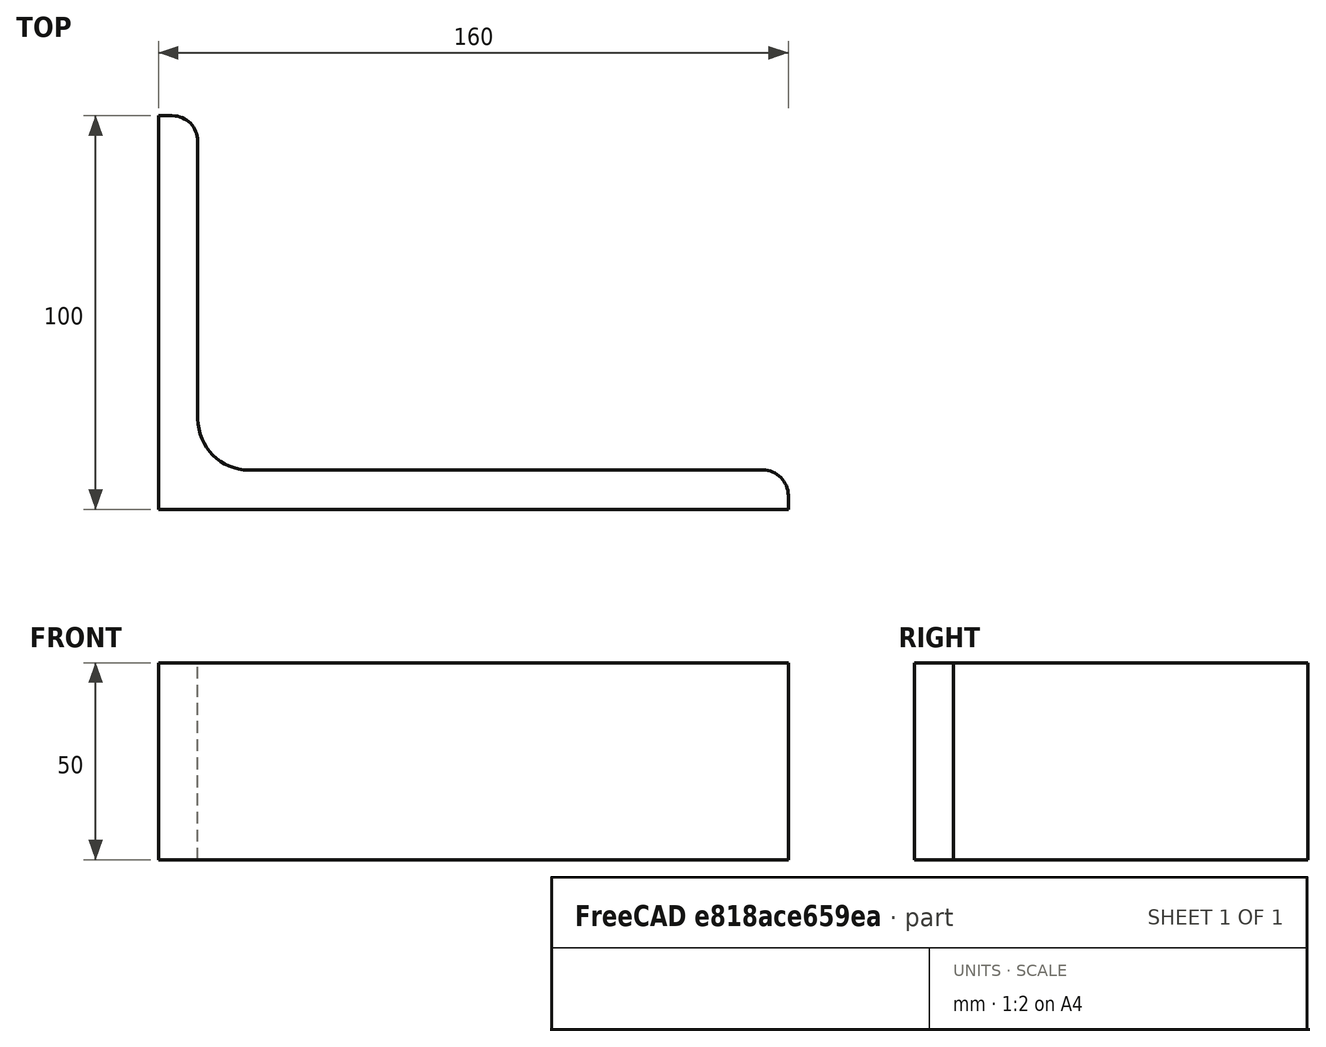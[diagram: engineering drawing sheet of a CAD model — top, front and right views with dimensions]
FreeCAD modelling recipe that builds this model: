
FCSTD DOCUMENT  (FreeCAD 0.15R4671 (Git))
Label: Angle Bar 160x100x10 EN10056 S235JR
License: All rights reserved
LicenseURL: http://en.wikipedia.org/wiki/All_rights_reserved
objects: Sketcher::SketchObject×1, Part::Extrusion×1
note: 2 computed .brp shape members not serialized (recipe doc carries the construction recipe); baked Part::Feature solids carry a one-line shape summary decoded from their .brp

FEATURE [Sketcher::SketchObject] Sketch
  sketch-geometry (9):
    g0: LineSegment StartX=0 StartY=0 StartZ=0 EndX=160 EndY=0 EndZ=0
    g1: LineSegment StartX=160 StartY=0 StartZ=0 EndX=160 EndY=3.5 EndZ=0
    g2: LineSegment StartX=153.5 StartY=10 StartZ=0 EndX=23 EndY=10 EndZ=0
    g3: LineSegment StartX=0 StartY=0 StartZ=0 EndX=0 EndY=100 EndZ=0
    g4: LineSegment StartX=0 StartY=100 StartZ=0 EndX=3.5 EndY=100 EndZ=0
    g5: LineSegment StartX=10 StartY=93.5 StartZ=0 EndX=10 EndY=23 EndZ=0
    g6: ArcOfCircle CenterX=23 CenterY=23 CenterZ=0 NormalX=0 NormalY=0 NormalZ=1 Radius=13 StartAngle=3.14159 EndAngle=4.71239
    g7: ArcOfCircle CenterX=3.5 CenterY=93.5 CenterZ=0 NormalX=0 NormalY=0 NormalZ=1 Radius=6.5 StartAngle=0 EndAngle=1.5708
    g8: ArcOfCircle CenterX=153.5 CenterY=3.5 CenterZ=0 NormalX=0 NormalY=0 NormalZ=1 Radius=6.5 StartAngle=0 EndAngle=1.5708
  constraints (23):
    c: Coincident(g0,g-1)
    c: Horizontal(g0)
    c: Coincident(g1,g0)
    c: Vertical(g1)
    c: Horizontal(g2)
    c: Coincident(g3,g-1)
    c: Vertical(g3)
    c: Coincident(g4,g3)
    c: Horizontal(g4)
    c: Vertical(g5)
    c: Tangent(g5,g6) = -1.5708
    c: Tangent(g2,g6) = 1.5708
    c: Tangent(g4,g7) = 1.5708
    c: Tangent(g5,g7) = 1.5708
    c: Tangent(g2,g8) = -1.5708
    c: Tangent(g1,g8) = -1.5708
    c: DistanceX(g0) = 160
    c: DistanceY(g3) = 100
    c: DistanceY(g0,g2) = 10
    c: DistanceX(g3,g5) = 10
    c: Radius(g6) = 13
    c: Radius(g8) = 6.5
    c: Radius(g7) = 6.5
FEATURE [Part::Extrusion] Extrude  label="Angle Bar 160x100x10 EN10056 S235JR"
  Base = -> Sketch
  Dir = (0,0,50)
  Solid = true
